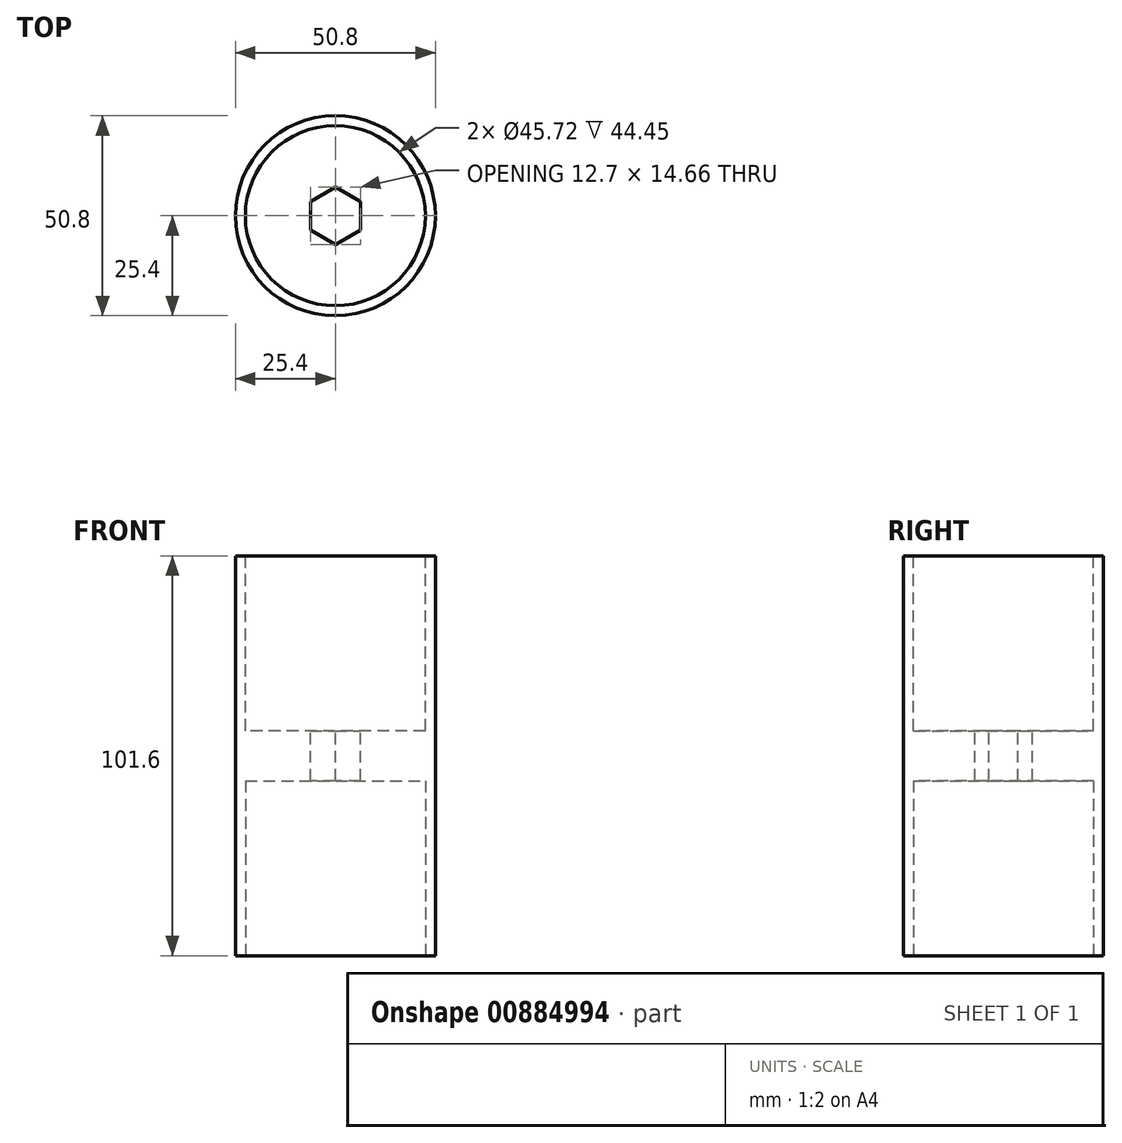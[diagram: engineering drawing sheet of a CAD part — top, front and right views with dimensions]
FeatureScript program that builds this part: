
annotation { "Feature Type Name" : "Feature", "Feature Type Description" : "" }
export const myFeature = defineFeature(function(context is Context, id is Id, definition is map)
    precondition{}
    {
        {
            var Q0;
            Q0=qCreatedBy(makeId("Top.planeOp"),FACE);
            var sketch = newSketch(context, id + "F0", { "sketchPlane" : qUnion([Q0])});
            skCircle(sketch, "E0", {"center": v(0, 0) * mm, "radius": 25.4 * mm});
            skSolve(sketch);
        }
        {
            var Q0;
            Q0 = qSketchRegion(id + "F0", true);
            extrude(context, id + "F1", {"entities" : qUnion([Q0]), "depth" : 101.6 * mm, "offsetDistance" : 25.4 * mm});
        }
        {
            var Q0;
            Q0=makeQuery(id+"F1.opExtrude","CAP_FACE",FACE,{"disambiguationData":[OSD([sQuery(id+"F0.wireOp",EDGE,"E0")])],"isStart":true});
            var sketch = newSketch(context, id + "F2", { "sketchPlane" : qUnion([Q0])});
            skCircle(sketch, "E1", {"center": v(0, 0) * mm, "radius": 22.86 * mm});
            skSolve(sketch);
        }
        {
            var Q0;
            Q0 = qSketchRegion(id + "F2", true);
            extrude(context, id + "F3", {"entities" : qUnion([Q0]), "operationType" : NewBodyOperationType.REMOVE, "oppositeDirection" : true, "depth" : 44.45 * mm, "offsetDistance" : 25.4 * mm});
        }
        {
            var Q0;
            Q0=makeQuery(id+"F1.opExtrude","CAP_FACE",FACE,{"disambiguationData":[OSD([sQuery(id+"F0.wireOp",EDGE,"E0")])],"isStart":false});
            var sketch = newSketch(context, id + "F4", { "sketchPlane" : qUnion([Q0])});
            skCircle(sketch, "E2", {"center": v(0, 0) * mm, "radius": 22.86 * mm});
            skSolve(sketch);
        }
        {
            var Q0;
            Q0 = qSketchRegion(id + "F4", true);
            extrude(context, id + "F5", {"entities" : qUnion([Q0]), "operationType" : NewBodyOperationType.REMOVE, "oppositeDirection" : true, "depth" : 44.45 * mm, "offsetDistance" : 25.4 * mm});
        }
        {
            var Q0;
            Q0=makeQuery(id+"F5.boolean.opBoolean","COPY",FACE,{"derivedFrom":makeQuery(id+"F5.opExtrude","CAP_FACE",FACE,{"disambiguationData":[OSD([sQuery(id+"F4.wireOp",EDGE,"E2")])],"isStart":false})});
            var sketch = newSketch(context, id + "F6", { "sketchPlane" : qUnion([Q0])});
            skCircle(sketch, "E3.cCircle", {"center": v(0, 0) * mm, "radius": 6.35 * mm, "construction": true});
            skLineSegment(sketch, "E3.0", {"start": v(0, 7.33) * mm, "end": v(6.35, 3.67) * mm});
            skLineSegment(sketch, "E3.1", {"start": v(6.35, 3.67) * mm, "end": v(6.35, -3.67) * mm});
            skLineSegment(sketch, "E3.2", {"start": v(6.35, -3.67) * mm, "end": v(0, -7.33) * mm});
            skLineSegment(sketch, "E3.3", {"start": v(0, -7.33) * mm, "end": v(-6.35, -3.67) * mm});
            skLineSegment(sketch, "E3.4", {"start": v(-6.35, -3.67) * mm, "end": v(-6.35, 3.67) * mm});
            skLineSegment(sketch, "E3.5", {"start": v(-6.35, 3.67) * mm, "end": v(0, 7.33) * mm});
            skPoint(sketch, "E3.0.midPoint", {"position": v(3.18, 5.5) * mm});
            skSolve(sketch);
        }
        {
            var Q0;
            Q0 = qSketchRegion(id + "F6", true);
            extrude(context, id + "F7", {"entities" : qUnion([Q0]), "operationType" : NewBodyOperationType.REMOVE, "endBound" : BoundingType.THROUGH_ALL, "oppositeDirection" : true, "depth" : 25.4 * mm, "offsetDistance" : 25.4 * mm});
        }
    });
